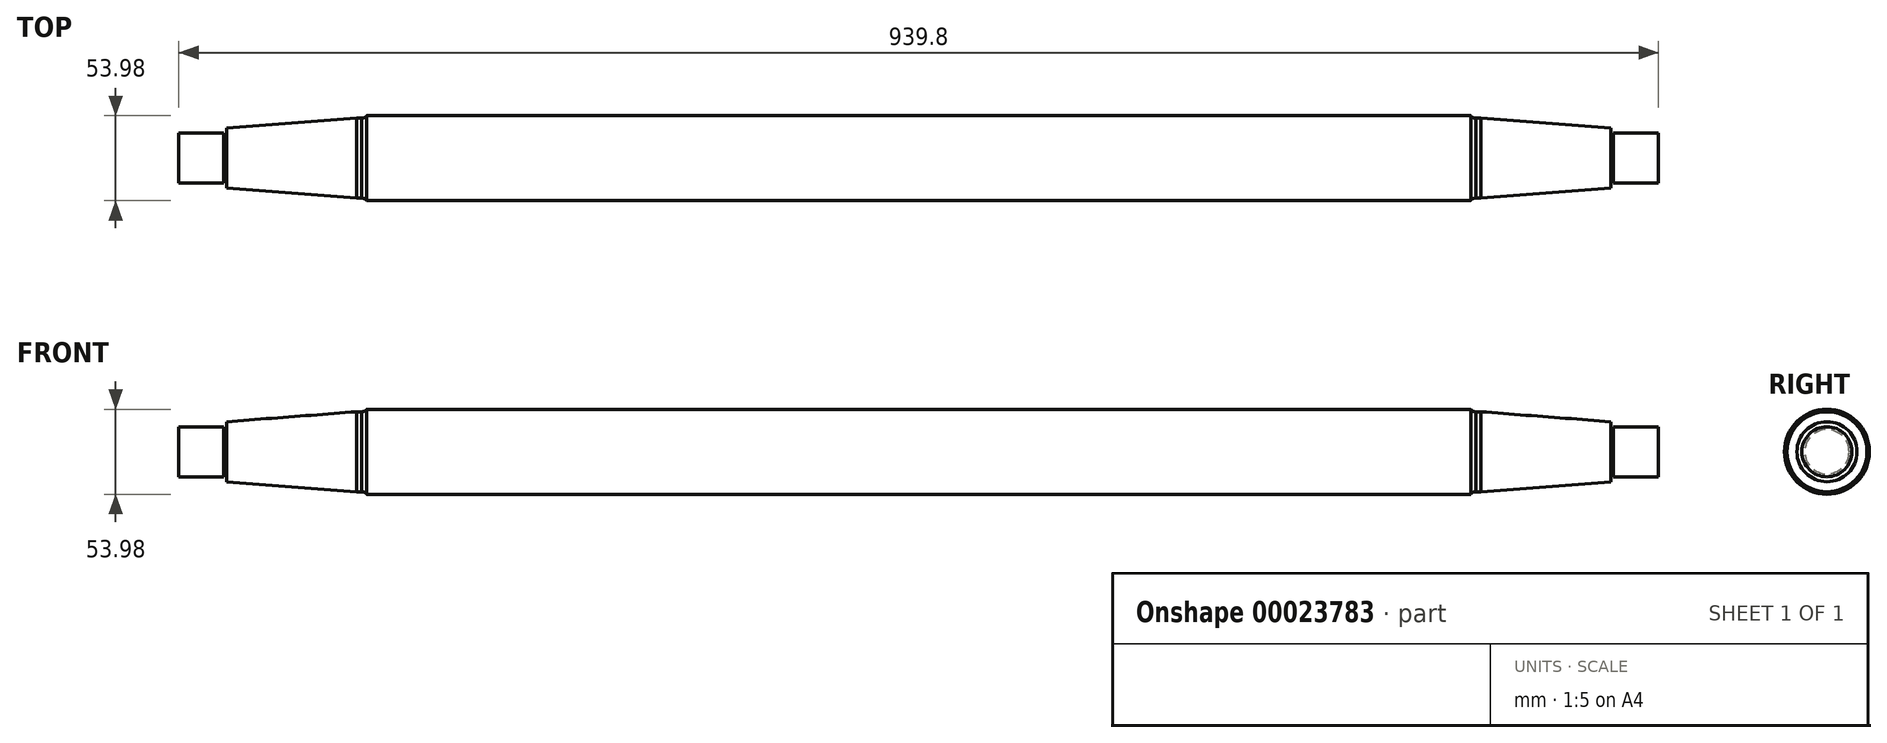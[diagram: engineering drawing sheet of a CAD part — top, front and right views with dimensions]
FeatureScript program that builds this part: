
annotation { "Feature Type Name" : "Feature", "Feature Type Description" : "" }
export const myFeature = defineFeature(function(context is Context, id is Id, definition is map)
    precondition{}
    {
        {
            var Q0;
            Q0=qCreatedBy(makeId("Front.planeOp"),FACE);
            var sketch = newSketch(context, id + "F0", { "sketchPlane" : qUnion([Q0])});
            skLineSegment(sketch, "E0", {"start": v(-469.9, 0) * mm, "end": v(469.9, 0) * mm});
            skLineSegment(sketch, "E1", {"start": v(0, 76.2) * mm, "end": v(0, -76.2) * mm, "construction": true});
            skLineSegment(sketch, "E2", {"start": v(-469.9, 0) * mm, "end": v(-469.9, 15.88) * mm});
            skLineSegment(sketch, "E3.0", {"start": v(-441.32, 14.1) * mm, "end": v(-441.32, 15.88) * mm});
            skLineSegment(sketch, "E4.0", {"start": v(-439.55, 14.1) * mm, "end": v(-439.55, 19.05) * mm});
            skLineSegment(sketch, "E5", {"start": v(-469.9, 15.88) * mm, "end": v(-441.32, 15.88) * mm});
            skLineSegment(sketch, "E6", {"start": v(-441.32, 14.1) * mm, "end": v(-439.55, 14.1) * mm});
            skLineSegment(sketch, "E7", {"start": v(-439.55, 19.05) * mm, "end": v(-357, 25.4) * mm});
            skPoint(sketch, "E8.orphan", {"position": v(-439.55, 0) * mm});
            skLineSegment(sketch, "E9.0", {"start": v(-350.65, 25.4) * mm, "end": v(-350.65, 26.99) * mm});
            skLineSegment(sketch, "E10", {"start": v(-357, 25.4) * mm, "end": v(-353.24, 25.4) * mm});
            skArc(sketch, "E11", {"start": v(-353.82, 25.4) * mm, "mid": v(-352.01, 25.75) * mm, "end": v(-350.65, 26.99) * mm});
            skPoint(sketch, "E12.orphan", {"position": v(-350.65, 25.4) * mm});
            skLineSegment(sketch, "E13", {"start": v(-350.65, 26.99) * mm, "end": v(0, 26.99) * mm});
            skLineSegment(sketch, "E14.MirrorCS", {"start": v(357, 25.4) * mm, "end": v(353.24, 25.4) * mm});
            skLineSegment(sketch, "E15.MirrorCS", {"start": v(350.65, 25.4) * mm, "end": v(350.65, 26.99) * mm});
            skArc(sketch, "E16.MirrorCS", {"start": v(353.82, 25.4) * mm, "mid": v(352.01, 25.75) * mm, "end": v(350.65, 26.99) * mm});
            skLineSegment(sketch, "E17.MirrorCS", {"start": v(441.32, 14.1) * mm, "end": v(441.32, 15.88) * mm});
            skLineSegment(sketch, "E18.MirrorCS", {"start": v(439.55, 14.1) * mm, "end": v(439.55, 19.05) * mm});
            skLineSegment(sketch, "E19.MirrorCS", {"start": v(441.32, 14.1) * mm, "end": v(439.55, 14.1) * mm});
            skLineSegment(sketch, "E20.MirrorCS", {"start": v(469.9, 0) * mm, "end": v(469.9, 15.88) * mm});
            skLineSegment(sketch, "E21.MirrorCS", {"start": v(469.9, 15.88) * mm, "end": v(441.32, 15.88) * mm});
            skLineSegment(sketch, "E22.MirrorCS", {"start": v(439.55, 19.05) * mm, "end": v(357, 25.4) * mm});
            skPoint(sketch, "E23.MirrorP", {"position": v(350.65, 25.4) * mm});
            skPoint(sketch, "E24.MirrorP", {"position": v(439.55, 0) * mm});
            skLineSegment(sketch, "E25.MirrorCS", {"start": v(350.65, 26.99) * mm, "end": v(0, 26.99) * mm});
            skSolve(sketch);
        }
        {
            var Q0;
            Q0=makeQuery(id+"F0.imprint","IMPRINT",FACE,{"disambiguationData":[TD([[makeQuery(id+"F0.imprint","IMPRINT",EDGE,{"derivedFrom":sQuery(id+"F0.wireOp",EDGE,"E0")}),1.0]])]});
            var Q1;
            Q1=sQuery(id+"F0.wireOp",EDGE,"E0");
            revolve(context, id + "F1", {"entities" : qUnion([Q0]), "axis" : qUnion([Q1]), "revolveType" : RevolveType.FULL});
        }
    });
